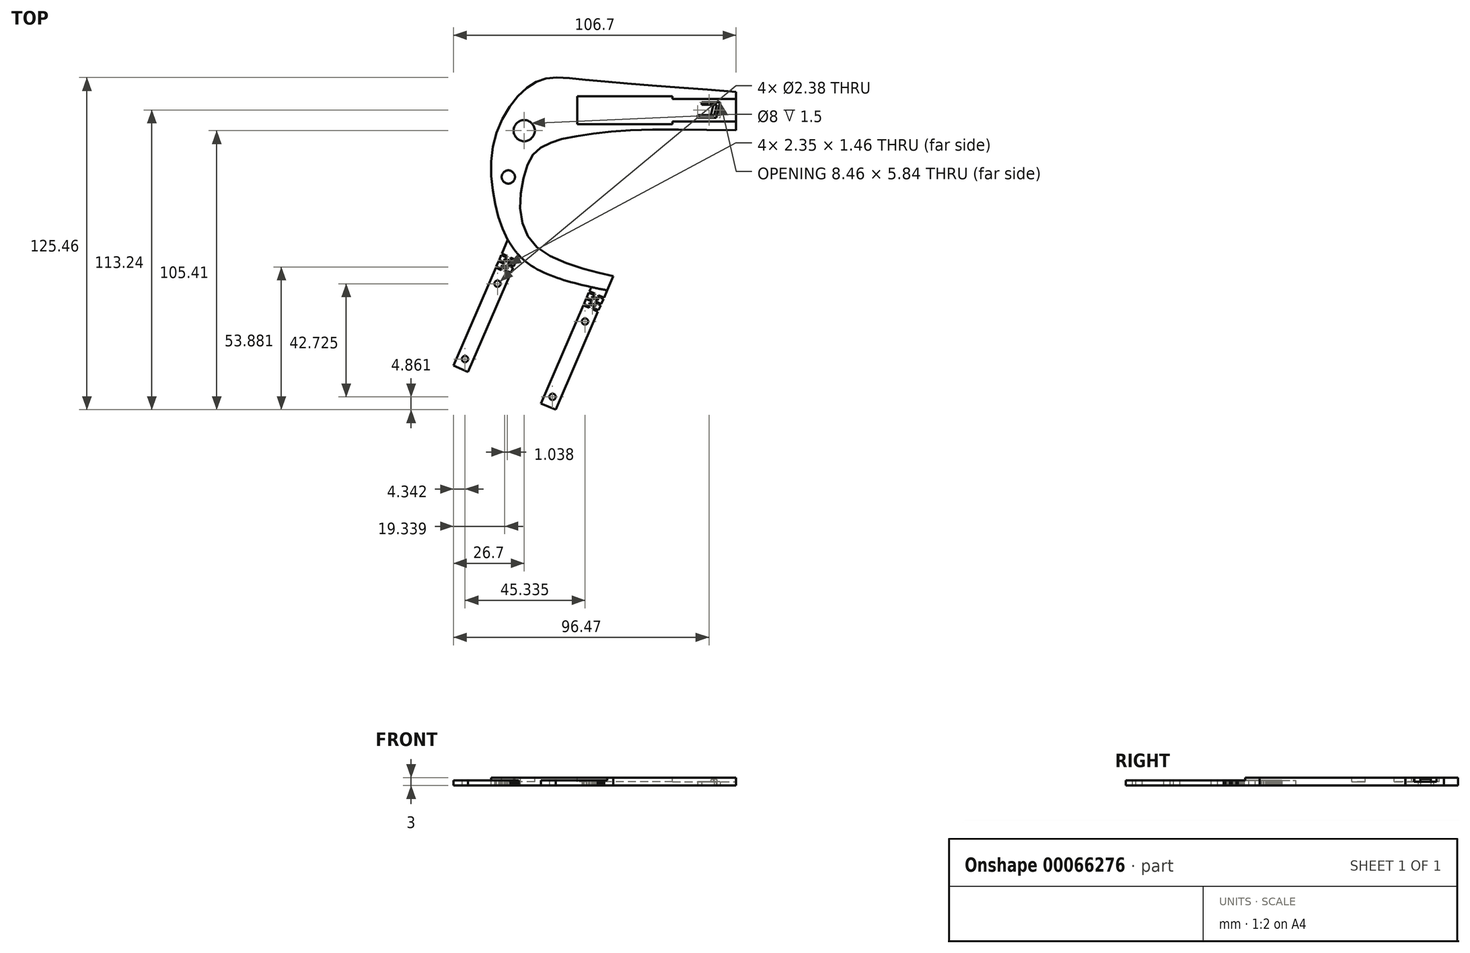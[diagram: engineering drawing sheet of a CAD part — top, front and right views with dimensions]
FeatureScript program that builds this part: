
annotation { "Feature Type Name" : "Feature", "Feature Type Description" : "" }
export const myFeature = defineFeature(function(context is Context, id is Id, definition is map)
    precondition{}
    {
        {
            var Q0;
            Q0=qCreatedBy(makeId("Top.planeOp"),FACE);
            var sketch = newSketch(context, id + "F0", { "sketchPlane" : qUnion([Q0])});
            skFitSpline(sketch, "E0", {"points": [v(28.77, -23.77) * mm, v(18.19, -21.23) * mm, v(4.66, -16.08) * mm, v(-3.14, -9.38) * mm, v(-6.2, -0.47) * mm, v(-5.92, 9.73) * mm, v(-3.32, 18.96) * mm, v(-0.42, 23.43) * mm, v(4.57, 26.35) * mm, v(10.6, 28.28) * mm, v(23.23, 30.26) * mm, v(40.55, 31.49) * mm, v(75.11, 31.25) * mm], "startDerivative": vector(-122, 25.6) * mm, "endDerivative": vector(252, -4.46) * mm});
            skFitSpline(sketch, "E1", {"points": [v(26.43, -29.18) * mm, v(12.1, -25.87) * mm, v(-3.17, -19.22) * mm, v(-12.01, -8.31) * mm, v(-16.51, 6.81) * mm, v(-16.39, 26.6) * mm, v(-7.91, 43.4) * mm, v(2.1, 50.5) * mm, v(16.74, 50.5) * mm, v(75.11, 45.84) * mm], "startDerivative": vector(-130.63, 24.59) * mm, "endDerivative": vector(348.84, -26.12) * mm});
            skLineSegment(sketch, "E2", {"start": v(75.11, 45.84) * mm, "end": v(75.11, 31.25) * mm});
            skLineSegment(sketch, "E3", {"start": v(28.77, -23.77) * mm, "end": v(6.98, -74.27) * mm});
            skLineSegment(sketch, "E4", {"start": v(6.98, -74.27) * mm, "end": v(1.47, -71.9) * mm});
            skLineSegment(sketch, "E5", {"start": v(1.47, -71.9) * mm, "end": v(20.43, -27.95) * mm});
            skLineSegment(sketch, "E6", {"start": v(-7, -15.8) * mm, "end": v(-26.08, -60) * mm});
            skLineSegment(sketch, "E7", {"start": v(-31.59, -57.63) * mm, "end": v(-11.08, -10.1) * mm});
            skLineSegment(sketch, "E8", {"start": v(66.87, 37.05) * mm, "end": v(60.65, 37.05) * mm});
            skLineSegment(sketch, "E9.0", {"start": v(67.65, 36.05) * mm, "end": v(60.65, 36.05) * mm});
            skLineSegment(sketch, "E9.2", {"start": v(69.11, 41.9) * mm, "end": v(62.11, 41.9) * mm});
            skLineSegment(sketch, "E10", {"start": v(60.65, 37.05) * mm, "end": v(60.65, 36.05) * mm});
            skCircle(sketch, "E11", {"center": v(5.8, -69.4) * mm, "radius": 1.2 * mm});
            skLineSegment(sketch, "E12", {"start": v(19.74, -29.54) * mm, "end": v(21.86, -30.45) * mm});
            skLineSegment(sketch, "E13", {"start": v(21.86, -30.45) * mm, "end": v(21.62, -31) * mm});
            skLineSegment(sketch, "E14", {"start": v(21.62, -31) * mm, "end": v(19.5, -30.09) * mm});
            skLineSegment(sketch, "E15", {"start": v(25.25, -31.91) * mm, "end": v(23.14, -31) * mm});
            skLineSegment(sketch, "E16", {"start": v(23.14, -31) * mm, "end": v(22.9, -31.55) * mm});
            skLineSegment(sketch, "E17", {"start": v(22.9, -31.55) * mm, "end": v(25.01, -32.46) * mm});
            skLineSegment(sketch, "E18", {"start": v(18.71, -31.92) * mm, "end": v(20.83, -32.83) * mm});
            skLineSegment(sketch, "E19", {"start": v(20.83, -32.83) * mm, "end": v(20.59, -33.39) * mm});
            skLineSegment(sketch, "E20", {"start": v(20.59, -33.39) * mm, "end": v(18.48, -32.47) * mm});
            skLineSegment(sketch, "E21", {"start": v(21.87, -33.94) * mm, "end": v(23.98, -34.85) * mm});
            skLineSegment(sketch, "E22", {"start": v(22.11, -33.39) * mm, "end": v(21.87, -33.94) * mm});
            skLineSegment(sketch, "E23", {"start": v(24.22, -34.3) * mm, "end": v(22.11, -33.39) * mm});
            skLineSegment(sketch, "E24", {"start": v(20.9, -31.45) * mm, "end": v(20.66, -32) * mm});
            skLineSegment(sketch, "E25", {"start": v(20.9, -31.45) * mm, "end": v(23.01, -32.36) * mm});
            skLineSegment(sketch, "E26", {"start": v(23.01, -32.36) * mm, "end": v(22.77, -32.91) * mm});
            skLineSegment(sketch, "E27", {"start": v(20.66, -32) * mm, "end": v(22.77, -32.91) * mm});
            skLineSegment(sketch, "E28", {"start": v(22, -34.76) * mm, "end": v(21.77, -35.31) * mm});
            skLineSegment(sketch, "E29", {"start": v(19.66, -34.4) * mm, "end": v(21.77, -35.31) * mm});
            skLineSegment(sketch, "E30", {"start": v(19.9, -33.85) * mm, "end": v(22, -34.76) * mm});
            skLineSegment(sketch, "E31", {"start": v(19.9, -33.85) * mm, "end": v(19.66, -34.4) * mm});
            skLineSegment(sketch, "E32", {"start": v(17.68, -34.31) * mm, "end": v(19.8, -35.22) * mm});
            skLineSegment(sketch, "E33", {"start": v(19.8, -35.22) * mm, "end": v(19.56, -35.77) * mm});
            skLineSegment(sketch, "E34", {"start": v(19.56, -35.77) * mm, "end": v(17.45, -34.86) * mm});
            skLineSegment(sketch, "E35", {"start": v(20.84, -36.33) * mm, "end": v(22.95, -37.24) * mm});
            skLineSegment(sketch, "E36", {"start": v(21.08, -35.78) * mm, "end": v(20.84, -36.33) * mm});
            skLineSegment(sketch, "E37", {"start": v(23.2, -36.69) * mm, "end": v(21.08, -35.78) * mm});
            skLineSegment(sketch, "E38", {"start": v(-13.33, -15.33) * mm, "end": v(-11.22, -16.24) * mm});
            skLineSegment(sketch, "E39", {"start": v(-11.22, -16.24) * mm, "end": v(-11.46, -16.79) * mm});
            skLineSegment(sketch, "E40", {"start": v(-11.46, -16.79) * mm, "end": v(-13.57, -15.88) * mm});
            skLineSegment(sketch, "E41", {"start": v(-7.82, -17.7) * mm, "end": v(-9.94, -16.8) * mm});
            skLineSegment(sketch, "E42", {"start": v(-9.94, -16.8) * mm, "end": v(-10.17, -17.34) * mm});
            skLineSegment(sketch, "E43", {"start": v(-10.17, -17.34) * mm, "end": v(-8.06, -18.25) * mm});
            skLineSegment(sketch, "E44", {"start": v(-12.15, -17.25) * mm, "end": v(-12.39, -17.8) * mm});
            skLineSegment(sketch, "E45", {"start": v(-12.15, -17.25) * mm, "end": v(-10.04, -18.16) * mm});
            skLineSegment(sketch, "E46", {"start": v(-10.04, -18.16) * mm, "end": v(-10.28, -18.71) * mm});
            skLineSegment(sketch, "E47", {"start": v(-12.39, -17.8) * mm, "end": v(-10.28, -18.71) * mm});
            skLineSegment(sketch, "E48", {"start": v(-12.49, -19.17) * mm, "end": v(-14.6, -18.26) * mm});
            skLineSegment(sketch, "E49", {"start": v(-12.25, -18.62) * mm, "end": v(-12.49, -19.17) * mm});
            skLineSegment(sketch, "E50", {"start": v(-14.36, -17.71) * mm, "end": v(-12.25, -18.62) * mm});
            skLineSegment(sketch, "E51", {"start": v(-10.97, -19.18) * mm, "end": v(-11.2, -19.73) * mm});
            skLineSegment(sketch, "E52", {"start": v(-8.85, -20.09) * mm, "end": v(-10.97, -19.18) * mm});
            skLineSegment(sketch, "E53", {"start": v(-11.2, -19.73) * mm, "end": v(-9.1, -20.64) * mm});
            skLineSegment(sketch, "E54", {"start": v(-13.19, -19.66) * mm, "end": v(-13.43, -20.2) * mm});
            skLineSegment(sketch, "E55", {"start": v(-13.19, -19.66) * mm, "end": v(-11.08, -20.57) * mm});
            skLineSegment(sketch, "E56", {"start": v(-11.08, -20.57) * mm, "end": v(-11.31, -21.12) * mm});
            skLineSegment(sketch, "E57", {"start": v(-13.43, -20.2) * mm, "end": v(-11.31, -21.12) * mm});
            skLineSegment(sketch, "E58", {"start": v(-15.4, -20.12) * mm, "end": v(-13.29, -21.03) * mm});
            skLineSegment(sketch, "E59", {"start": v(-13.29, -21.03) * mm, "end": v(-13.53, -21.58) * mm});
            skLineSegment(sketch, "E60", {"start": v(-13.53, -21.58) * mm, "end": v(-15.64, -20.67) * mm});
            skLineSegment(sketch, "E61", {"start": v(-12.24, -22.14) * mm, "end": v(-10.13, -23.05) * mm});
            skLineSegment(sketch, "E62", {"start": v(-12, -21.58) * mm, "end": v(-12.24, -22.14) * mm});
            skLineSegment(sketch, "E63", {"start": v(-9.9, -22.5) * mm, "end": v(-12, -21.58) * mm});
            skCircle(sketch, "E64", {"center": v(-27.25, -55.15) * mm, "radius": 1.2 * mm});
            skLineSegment(sketch, "E65", {"start": v(69.11, 41.9) * mm, "end": v(69.11, 33.9) * mm});
            skLineSegment(sketch, "E66", {"start": v(69.11, 33.9) * mm, "end": v(67.11, 33.9) * mm});
            skLineSegment(sketch, "E67", {"start": v(69.11, 41.9) * mm, "end": v(67.65, 36.05) * mm});
            skLineSegment(sketch, "E68", {"start": v(62.11, 41.9) * mm, "end": v(62.11, 40.9) * mm});
            skLineSegment(sketch, "E69", {"start": v(62.11, 40.9) * mm, "end": v(67.83, 40.9) * mm});
            skLineSegment(sketch, "E70", {"start": v(67.83, 40.9) * mm, "end": v(66.87, 37.05) * mm});
            skLineSegment(sketch, "E71.trimOffspring", {"start": v(-26.08, -60) * mm, "end": v(-31.59, -57.63) * mm});
            skCircle(sketch, "E72", {"center": v(-14.97, -26.68) * mm, "radius": 1.2 * mm});
            skCircle(sketch, "E73", {"center": v(18.09, -40.95) * mm, "radius": 1.2 * mm});
            skSolve(sketch);
        }
        {
            var Q0;
            {var subQ1=sQuery(id+"F0.wireOp",EDGE,"E0");Q0=makeQuery(id+"F0.imprint","IMPRINT",FACE,{"disambiguationData":[TD([[makeQuery(id+"F0.imprint","IMPRINT",EDGE,{"derivedFrom":subQ1}),1.0]])]});}
            extrude(context, id + "F1", {"entities" : qUnion([Q0]), "depth" : 3 * mm});
        }
        {
            var Q0;
            Q0=makeQuery(id+"F1.opExtrude","SWEPT_FACE",FACE,{"disambiguationData":[OSD([sQuery(id+"F0.wireOp",EDGE,"E2")])]});
            var sketch = newSketch(context, id + "F2", { "sketchPlane" : qUnion([Q0])});
            skLineSegment(sketch, "E74", {"start": v(43.14, 3) * mm, "end": v(43.14, 1.5) * mm});
            skPoint(sketch, "E74.endSnap0", {"position": v(45.84, 1.5) * mm});
            skLineSegment(sketch, "E75", {"start": v(43.14, 1.5) * mm, "end": v(34.64, 1.5) * mm});
            skLineSegment(sketch, "E76", {"start": v(34.64, 1.5) * mm, "end": v(34.64, 3) * mm});
            skLineSegment(sketch, "E77", {"start": v(34.64, 3) * mm, "end": v(43.14, 3) * mm});
            skSolve(sketch);
        }
        {
            var Q0;
            Q0=makeQuery(id+"F2.imprint","IMPRINT",FACE,{"disambiguationData":[TD([[makeQuery(id+"F2.imprint","IMPRINT",EDGE,{"derivedFrom":sQuery(id+"F2.wireOp",EDGE,"E74")}),-1.0]])]});
            extrude(context, id + "F3", {"entities" : qUnion([Q0]), "operationType" : NewBodyOperationType.REMOVE, "oppositeDirection" : true, "depth" : 60 * mm});
        }
        {
            var Q0;
            {var subQ15=sQuery(id+"F0.wireOp",EDGE,"E38");Q0=makeQuery(id+"F0.imprint","IMPRINT",FACE,{"disambiguationData":[TD([[makeQuery(id+"F0.imprint","IMPRINT",EDGE,{"derivedFrom":subQ15}),1.0]])]});}
            var Q1;
            Q1=makeQuery(id+"F0.imprint","IMPRINT",FACE,{"disambiguationData":[TD([[makeQuery(id+"F0.imprint","IMPRINT",EDGE,{"derivedFrom":sQuery(id+"F0.wireOp",EDGE,"E11")}),-1.0]])]});
            extrude(context, id + "F4", {"entities" : qUnion([Q0, Q1]), "operationType" : NewBodyOperationType.ADD, "depth" : 2 * mm});
        }
        {
            var Q0;
            Q0=makeQuery(id+"F3.boolean.opBoolean","COPY",FACE,{"derivedFrom":makeQuery(id+"F3.opExtrude","SWEPT_FACE",FACE,{"disambiguationData":[OSD([sQuery(id+"F2.wireOp",EDGE,"E75")])]})});
            var sketch = newSketch(context, id + "F5", { "sketchPlane" : qUnion([Q0])});
            skLineSegment(sketch, "E78", {"start": v(65.61, 37.05) * mm, "end": v(66.57, 40.9) * mm});
            skSolve(sketch);
        }
        {
            var Q0;
            {var subQ0=sQuery(id+"F5.wireOp",EDGE,"E78");Q0=makeQuery(id+"F5.imprint","IMPRINT",FACE,{"disambiguationData":[TD([[makeQuery(id+"F5.imprint","IMPRINT",EDGE,{"derivedFrom":subQ0}),-1.0]])]});}
            extrude(context, id + "F6", {"entities" : qUnion([Q0]), "operationType" : NewBodyOperationType.ADD, "depth" : 1 * mm});
        }
        {
            var Q0;
            Q0=makeQuery(id+"F6.opExtrude","CAP_EDGE",EDGE,{"disambiguationData":[OSD([sQuery(id+"F0.wireOp",EDGE,"E70"),sQuery(id+"F2.wireOp",EDGE,"E75")])],"isStart":false});
            var Q1;
            Q1=makeQuery(id+"F6.opExtrude","CAP_EDGE",EDGE,{"disambiguationData":[OSD([sQuery(id+"F5.wireOp",EDGE,"E78")])],"isStart":false});
            fillet(context, id + "F7", {"entities" : qUnion([Q0, Q1]), "radius" : .5 * mm, "tangentPropagation" : true, "allowEdgeOverflow" : false});
        }
        {
            var Q0;
            Q0=makeQuery(id+"F1.opExtrude","CAP_FACE",FACE,{"disambiguationData":[OSD([sQuery(id+"F0.wireOp",EDGE,"E0"),sQuery(id+"F0.wireOp",EDGE,"E1"),sQuery(id+"F0.wireOp",EDGE,"E2"),sQuery(id+"F0.wireOp",EDGE,"E3"),sQuery(id+"F0.wireOp",EDGE,"E8"),sQuery(id+"F0.wireOp",EDGE,"E9.0"),sQuery(id+"F0.wireOp",EDGE,"E9.2"),sQuery(id+"F0.wireOp",EDGE,"E10"),sQuery(id+"F0.wireOp",EDGE,"E67"),sQuery(id+"F0.wireOp",EDGE,"E68"),sQuery(id+"F0.wireOp",EDGE,"E69"),sQuery(id+"F0.wireOp",EDGE,"E70")])],"isStart":false});
            var sketch = newSketch(context, id + "F8", { "sketchPlane" : qUnion([Q0])});
            skLineSegment(sketch, "E79.bottom", {"start": v(51.11, 44.14) * mm, "end": v(15.11, 44.14) * mm});
            skLineSegment(sketch, "E79.top", {"start": v(51.11, 33.64) * mm, "end": v(15.11, 33.64) * mm});
            skLineSegment(sketch, "E79.left", {"start": v(51.11, 44.14) * mm, "end": v(51.11, 33.64) * mm});
            skLineSegment(sketch, "E79.right", {"start": v(15.11, 44.14) * mm, "end": v(15.11, 33.64) * mm});
            skCircle(sketch, "E80", {"center": v(-4.89, 31.14) * mm, "radius": 4 * mm});
            skCircle(sketch, "E81", {"center": v(-10.89, 13.64) * mm, "radius": 2.5 * mm});
            skSolve(sketch);
        }
        {
            var Q0;
            {var subQ0=sQuery(id+"F8.wireOp",EDGE,"E79.top");Q0=makeQuery(id+"F8.imprint","IMPRINT",FACE,{"disambiguationData":[TD([[makeQuery(id+"F8.imprint","IMPRINT",EDGE,{"derivedFrom":subQ0}),-1.0]])]});}
            var Q1;
            {var subQ0=sQuery(id+"F8.wireOp",EDGE,"E79.bottom");Q1=makeQuery(id+"F8.imprint","IMPRINT",FACE,{"disambiguationData":[TD([[makeQuery(id+"F8.imprint","IMPRINT",EDGE,{"derivedFrom":subQ0}),1.0]])]});}
            var Q2;
            Q2=makeQuery(id+"F8.imprint","IMPRINT",FACE,{"disambiguationData":[TD([[makeQuery(id+"F8.imprint","IMPRINT",EDGE,{"derivedFrom":sQuery(id+"F8.wireOp",EDGE,"E80")}),1.0]])]});
            var Q3;
            Q3=makeQuery(id+"F8.imprint","IMPRINT",FACE,{"disambiguationData":[TD([[makeQuery(id+"F8.imprint","IMPRINT",EDGE,{"derivedFrom":sQuery(id+"F8.wireOp",EDGE,"E81")}),1.0]])]});
            extrude(context, id + "F9", {"entities" : qUnion([Q0, Q1, Q2, Q3]), "operationType" : NewBodyOperationType.REMOVE, "oppositeDirection" : true, "depth" : 1.5 * mm});
        }
    });
